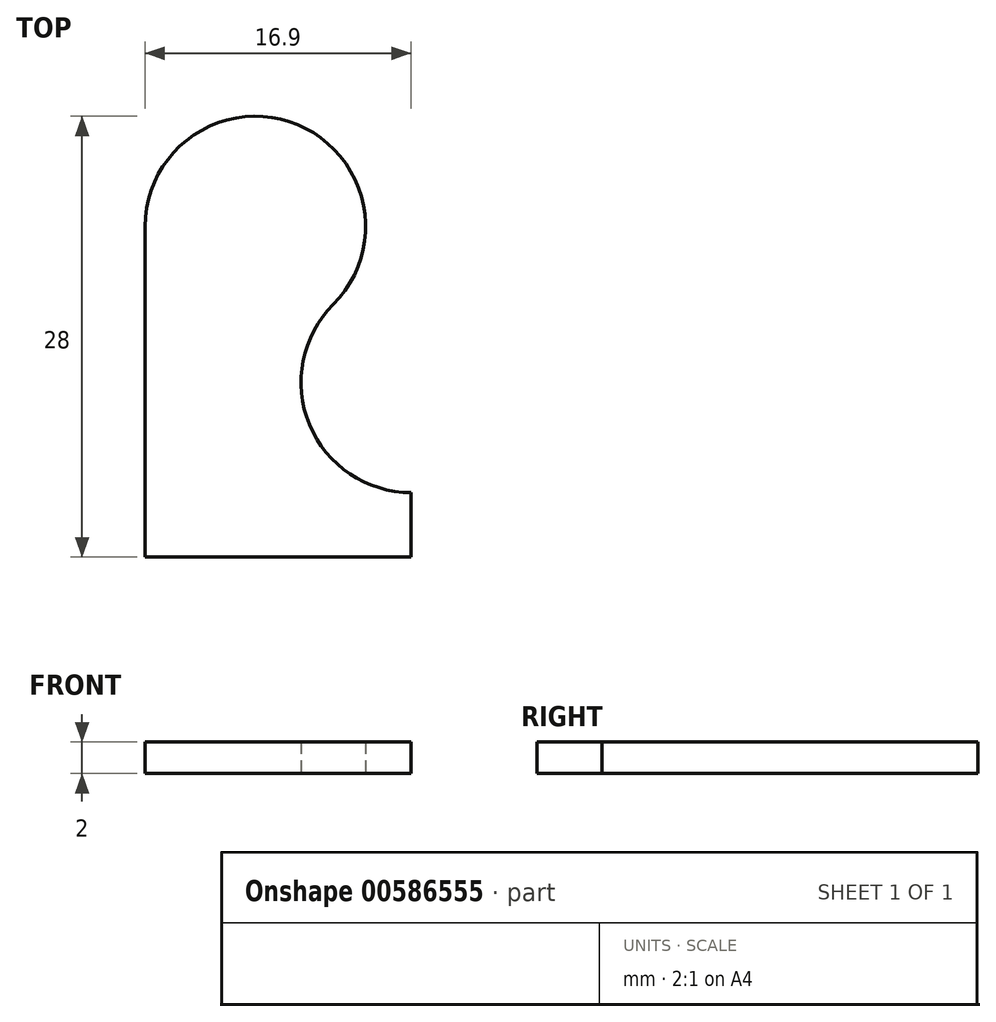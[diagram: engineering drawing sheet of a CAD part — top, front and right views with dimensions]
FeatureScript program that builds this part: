
annotation { "Feature Type Name" : "Feature", "Feature Type Description" : "" }
export const myFeature = defineFeature(function(context is Context, id is Id, definition is map)
    precondition{}
    {
        {
            var Q0;
            Q0=qCreatedBy(makeId("Top.planeOp"),FACE);
            var sketch = newSketch(context, id + "F0", { "sketchPlane" : qUnion([Q0])});
            skLineSegment(sketch, "E0", {"start": v(0, 0) * mm, "end": v(0, 21) * mm});
            skArc(sketch, "E1", {"start": v(0, 21) * mm, "mid": v(9.68, 27.47) * mm, "end": v(11.95, 16.05) * mm});
            skArc(sketch, "E2", {"start": v(11.95, 16.05) * mm, "mid": v(10.43, 8.42) * mm, "end": v(16.9, 4.1) * mm});
            skLineSegment(sketch, "E3", {"start": v(7, 21) * mm, "end": v(16.9, 11.1) * mm, "construction": true});
            skLineSegment(sketch, "E4", {"start": v(16.9, 0) * mm, "end": v(16.9, 11.1) * mm, "construction": true});
            skLineSegment(sketch, "E5", {"start": v(0, 0) * mm, "end": v(16.9, 0) * mm});
            skLineSegment(sketch, "E6", {"start": v(16.9, 4.1) * mm, "end": v(16.9, 0) * mm});
            skLineSegment(sketch, "E7", {"start": v(0, 21) * mm, "end": v(7, 21) * mm, "construction": true});
            skLineSegment(sketch, "E8", {"start": v(7, 21) * mm, "end": v(7, 14) * mm, "construction": true});
            skLineSegment(sketch, "E9", {"start": v(7, 14) * mm, "end": v(7, 7) * mm, "construction": true});
            skLineSegment(sketch, "E10", {"start": v(7, 0) * mm, "end": v(7, 7) * mm, "construction": true});
            skSolve(sketch);
        }
        {
            var Q0;
            Q0=qSketchRegion(id+"F0",true);
            extrude(context, id + "F1", {"entities" : qUnion([Q0]), "depth" : 2 * mm, "offsetDistance" : 25 * mm});
        }
    });
